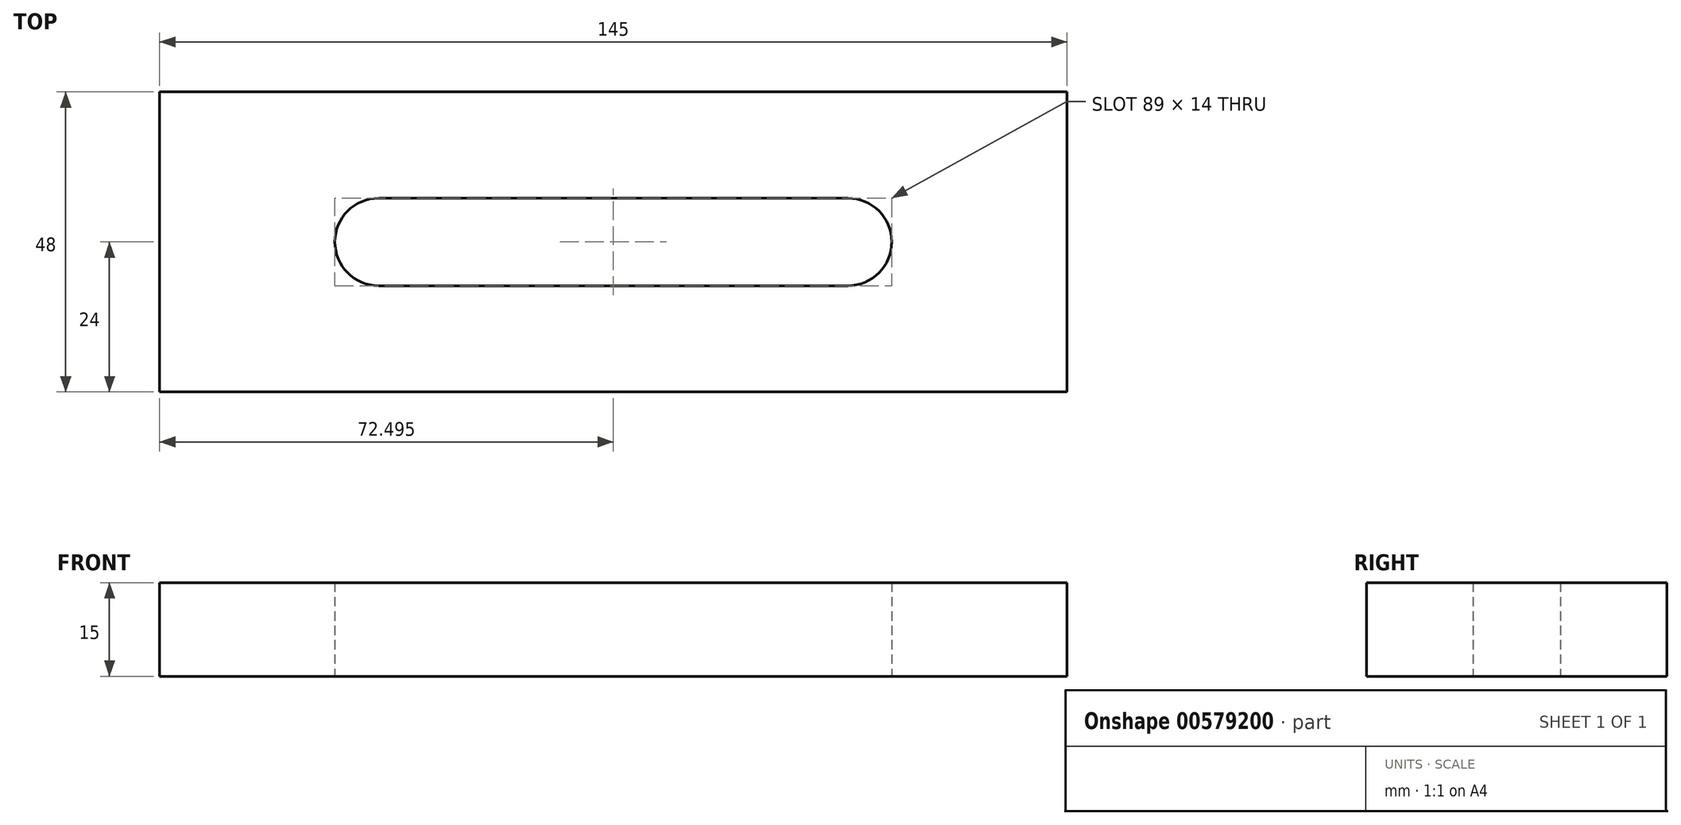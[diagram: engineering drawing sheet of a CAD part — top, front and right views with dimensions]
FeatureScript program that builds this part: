
annotation { "Feature Type Name" : "Feature", "Feature Type Description" : "" }
export const myFeature = defineFeature(function(context is Context, id is Id, definition is map)
    precondition{}
    {
        {
            var Q0;
            Q0=qCreatedBy(makeId("Top.planeOp"),FACE);
            var sketch = newSketch(context, id + "F0", { "sketchPlane" : qUnion([Q0])});
            skLineSegment(sketch, "E0", {"start": v(-62.6, 0) * mm, "end": v(-62.6, -48) * mm});
            skLineSegment(sketch, "E1", {"start": v(-62.6, -48) * mm, "end": v(82.4, -48) * mm});
            skLineSegment(sketch, "E2", {"start": v(82.4, -48) * mm, "end": v(82.4, 0) * mm});
            skLineSegment(sketch, "E3", {"start": v(82.4, 0) * mm, "end": v(-62.6, 0) * mm});
            skArc(sketch, "E4", {"start": v(-27.6, -17) * mm, "mid": v(-34.6, -24) * mm, "end": v(-27.6, -31) * mm});
            skArc(sketch, "E5", {"start": v(47.4, -31) * mm, "mid": v(54.4, -24) * mm, "end": v(47.4, -17) * mm});
            skLineSegment(sketch, "E6", {"start": v(-27.6, -17) * mm, "end": v(47.4, -17) * mm});
            skLineSegment(sketch, "E7", {"start": v(-27.6, -31) * mm, "end": v(47.4, -31) * mm});
            skSolve(sketch);
        }
        {
            var Q0;
            Q0 = qSketchRegion(id + "F0", true);
            extrude(context, id + "F1", {"entities" : qUnion([Q0]), "depth" : 15 * mm, "offsetDistance" : 25 * mm});
        }
        {
            var Q0;
            Q0=qCreatedBy(makeId("Top.planeOp"),FACE);
            var sketch = newSketch(context, id + "F2", { "sketchPlane" : qUnion([Q0])});
            skLineSegment(sketch, "E8", {"start": v(-62.6, -12) * mm, "end": v(82.4, -12) * mm});
            skLineSegment(sketch, "E9", {"start": v(82.4, -12) * mm, "end": v(82.4, 0) * mm});
            skLineSegment(sketch, "E10", {"start": v(82.4, 0) * mm, "end": v(-62.6, 0) * mm});
            skLineSegment(sketch, "E11", {"start": v(-62.6, 0) * mm, "end": v(-62.6, -12) * mm});
            skSolve(sketch);
        }
        {
            var Q0;
            Q0 = qSketchRegion(id + "F2", true);
            extrude(context, id + "F3", {"entities" : qUnion([Q0]), "operationType" : NewBodyOperationType.ADD, "depth" : 15 * mm, "offsetDistance" : 25 * mm});
        }
    });
